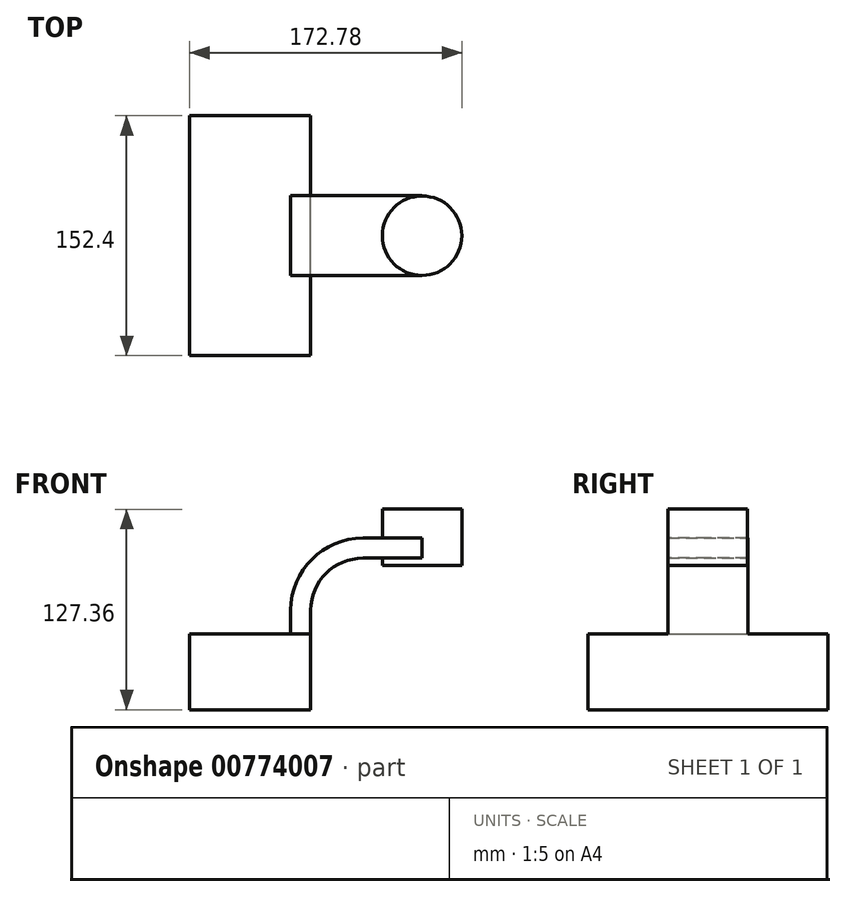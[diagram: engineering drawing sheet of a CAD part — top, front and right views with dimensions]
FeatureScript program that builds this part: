
annotation { "Feature Type Name" : "Feature", "Feature Type Description" : "" }
export const myFeature = defineFeature(function(context is Context, id is Id, definition is map)
    precondition{}
    {
        {
            var Q0;
            Q0=qCreatedBy(makeId("Front.planeOp"),FACE);
            var sketch = newSketch(context, id + "F0", { "sketchPlane" : qUnion([Q0])});
            skLineSegment(sketch, "E0.bottom", {"start": v(-33.65, 21.17) * mm, "end": v(43.21, 21.17) * mm});
            skLineSegment(sketch, "E0.top", {"start": v(-33.65, -27.11) * mm, "end": v(43.21, -27.11) * mm});
            skLineSegment(sketch, "E0.left", {"start": v(-33.65, 21.17) * mm, "end": v(-33.65, -27.11) * mm});
            skLineSegment(sketch, "E0.right", {"start": v(43.21, 21.17) * mm, "end": v(43.21, -27.11) * mm});
            skLineSegment(sketch, "E1.bottom", {"start": v(91.8, 100.25) * mm, "end": v(139.13, 100.25) * mm});
            skLineSegment(sketch, "E1.top", {"start": v(91.8, 64.68) * mm, "end": v(139.13, 64.68) * mm});
            skLineSegment(sketch, "E1.left", {"start": v(91.8, 100.25) * mm, "end": v(91.8, 64.68) * mm});
            skLineSegment(sketch, "E1.right", {"start": v(139.13, 100.25) * mm, "end": v(139.13, 64.68) * mm});
            skLineSegment(sketch, "E2", {"start": v(43.21, 21.17) * mm, "end": v(43.21, 36.13) * mm});
            skArc(sketch, "E3", {"start": v(43.21, 36.13) * mm, "mid": v(52.89, 59.49) * mm, "end": v(76.25, 69.16) * mm});
            skLineSegment(sketch, "E4", {"start": v(76.25, 69.16) * mm, "end": v(113.9, 69.16) * mm});
            skLineSegment(sketch, "E5.0", {"start": v(76.25, 81.86) * mm, "end": v(113.9, 81.86) * mm});
            skArc(sketch, "E5.1", {"start": v(30.51, 36.13) * mm, "mid": v(43.9, 68.47) * mm, "end": v(76.25, 81.86) * mm});
            skLineSegment(sketch, "E5.2", {"start": v(30.51, 21.17) * mm, "end": v(30.51, 36.13) * mm});
            skLineSegment(sketch, "E6", {"start": v(113.9, 69.16) * mm, "end": v(113.9, 100.25) * mm});
            skLineSegment(sketch, "E7", {"start": v(113.9, 69.16) * mm, "end": v(113.9, 64.68) * mm});
            skFitSpline(sketch, "E8", {"points": [v(-33.65, 21.17) * mm, v(76.25, 81.86) * mm], "startDerivative": vector(71.06, 83.97) * mm, "endDerivative": vector(182.05, -4.25) * mm});
            skSolve(sketch);
        }
        {
            var Q0;
            Q0=makeQuery(id+"F0.imprint","IMPRINT",FACE,{"disambiguationData":[TD([[makeQuery(id+"F0.imprint","IMPRINT",EDGE,{"derivedFrom":sQuery(id+"F0.wireOp",EDGE,"E0.top")}),1.0]])]});
            extrude(context, id + "F1", {"entities" : qUnion([Q0]), "endBound" : BoundingType.SYMMETRIC, "depth" : 152.4 * mm, "offsetDistance" : 25.4 * mm});
        }
        {
            var Q0;
            {var subQ0=sQuery(id+"F0.wireOp",EDGE,"E5.0");var subQ1=sQuery(id+"F0.wireOp",EDGE,"E1.left");var subQ2=makeQuery(id+"F0.imprint","INTERSECT",VERTEX,{"derivedFrom":[subQ1,subQ0]});Q0=makeQuery(id+"F0.imprint","IMPRINT",FACE,{"disambiguationData":[TD([[makeQuery(id+"F0.imprint","IMPRINT",EDGE,{"disambiguationData":[TD([[subQ2,-1.0]])],"derivedFrom":subQ1}),1.0]])]});}
            var Q1;
            {var subQ1=sQuery(id+"F0.wireOp",EDGE,"E2");Q1=makeQuery(id+"F0.imprint","IMPRINT",FACE,{"disambiguationData":[TD([[makeQuery(id+"F0.imprint","IMPRINT",EDGE,{"derivedFrom":subQ1}),1.0]])]});}
            extrude(context, id + "F2", {"entities" : qUnion([Q0, Q1]), "operationType" : NewBodyOperationType.ADD, "endBound" : BoundingType.SYMMETRIC, "depth" : 50.8 * mm, "offsetDistance" : 25.4 * mm});
        }
        {
            var Q0;
            Q0=sQuery(id+"F0.wireOp",EDGE,"E8");
            extrude(context, id + "F3", {"bodyType" : ToolBodyType.SURFACE, "surfaceEntities" : qUnion([Q0]), "endBound" : BoundingType.SYMMETRIC, "depth" : 12.7 * mm, "offsetDistance" : 25.4 * mm});
        }
        {
            var Q0;
            Q0=makeQuery(id+"F0.imprint","IMPRINT",FACE,{"disambiguationData":[TD([[makeQuery(id+"F0.imprint","IMPRINT",EDGE,{"derivedFrom":sQuery(id+"F0.wireOp",EDGE,"E5.1")}),1.0]])]});
            extrude(context, id + "F4", {"entities" : qUnion([Q0]), "operationType" : NewBodyOperationType.ADD, "endBound" : BoundingType.SYMMETRIC, "depth" : 12.7 * mm, "offsetDistance" : 25.4 * mm});
        }
        {
            var Q0;
            {var subQ0=sQuery(id+"F0.wireOp",EDGE,"E1.right");Q0=makeQuery(id+"F0.imprint","IMPRINT",FACE,{"disambiguationData":[TD([[makeQuery(id+"F0.imprint","IMPRINT",EDGE,{"derivedFrom":subQ0}),-1.0]])]});}
            var Q1;
            Q1=sQuery(id+"F0.wireOp",EDGE,"E6");
            revolve(context, id + "F5", {"operationType" : NewBodyOperationType.ADD, "surfaceOperationType" : NewSurfaceOperationType.NEW, "entities" : qUnion([Q0]), "axis" : qUnion([Q1]), "revolveType" : RevolveType.FULL});
        }
    });
